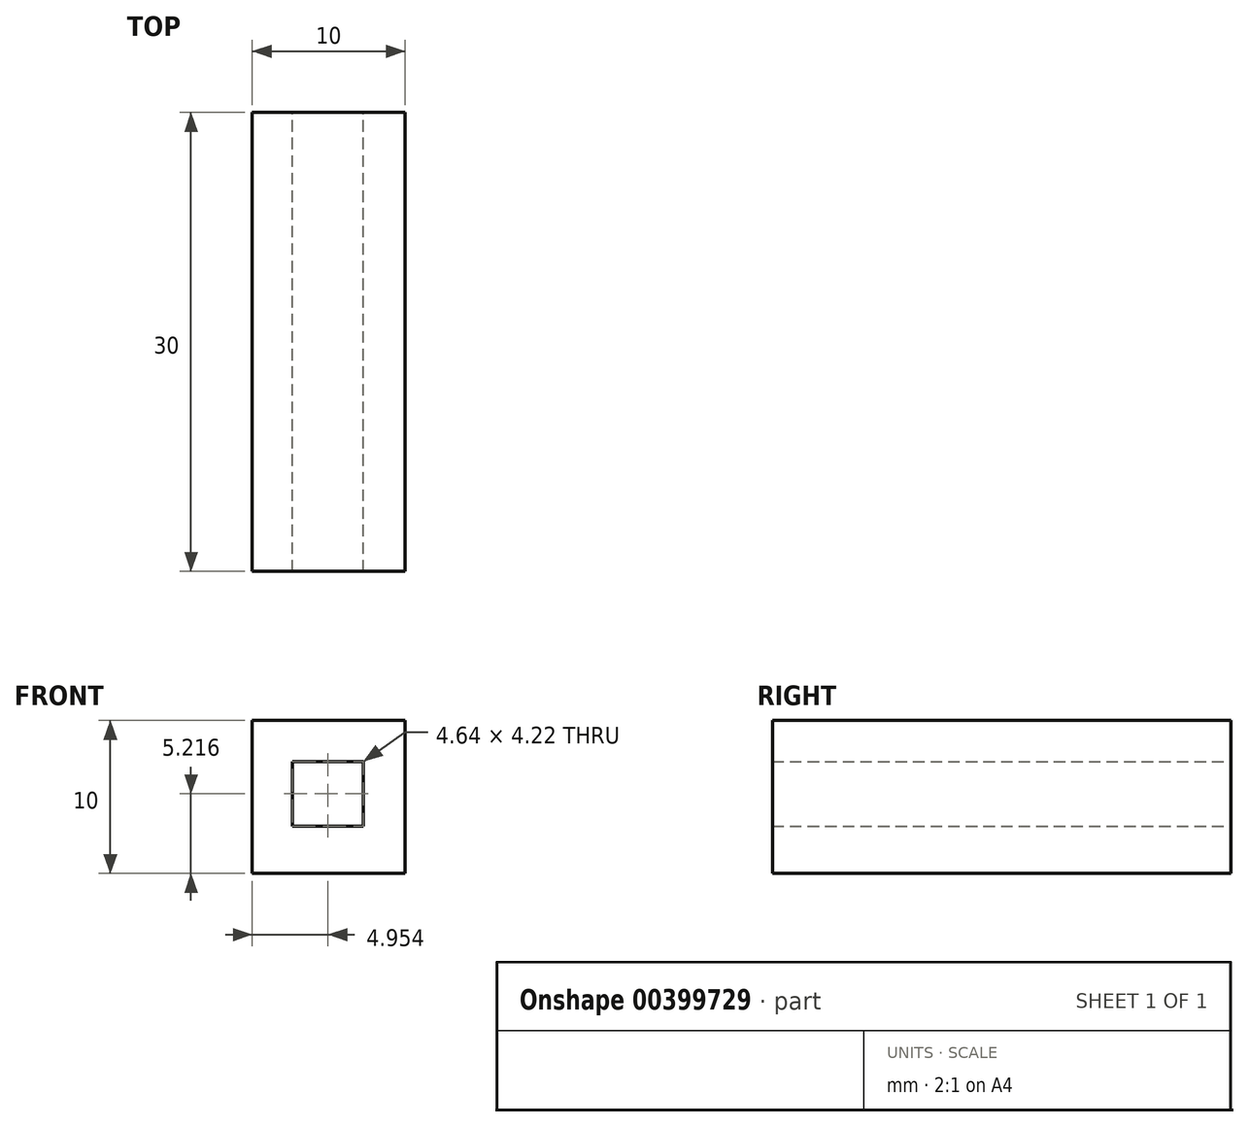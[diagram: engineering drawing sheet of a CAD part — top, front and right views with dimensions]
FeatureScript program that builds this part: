
annotation { "Feature Type Name" : "Feature", "Feature Type Description" : "" }
export const myFeature = defineFeature(function(context is Context, id is Id, definition is map)
    precondition{}
    {
        {
            var Q0;
            Q0=qCreatedBy(makeId("Front.planeOp"),FACE);
            var sketch = newSketch(context, id + "F0", { "sketchPlane" : qUnion([Q0])});
            skLineSegment(sketch, "E0.bottom", {"start": v(-17.14, 25.4) * mm, "end": v(-7.14, 25.4) * mm});
            skLineSegment(sketch, "E0.top", {"start": v(-17.14, 15.4) * mm, "end": v(-7.14, 15.4) * mm});
            skLineSegment(sketch, "E0.left", {"start": v(-17.14, 25.4) * mm, "end": v(-17.14, 15.4) * mm});
            skLineSegment(sketch, "E0.right", {"start": v(-7.14, 25.4) * mm, "end": v(-7.14, 15.4) * mm});
            skLineSegment(sketch, "E1.bottom", {"start": v(-14.5, 22.72) * mm, "end": v(-9.87, 22.72) * mm});
            skLineSegment(sketch, "E1.top", {"start": v(-14.5, 18.5) * mm, "end": v(-9.87, 18.5) * mm});
            skLineSegment(sketch, "E1.left", {"start": v(-14.5, 22.72) * mm, "end": v(-14.5, 18.5) * mm});
            skLineSegment(sketch, "E1.right", {"start": v(-9.87, 22.72) * mm, "end": v(-9.87, 18.5) * mm});
            skSolve(sketch);
        }
        {
            var Q0;
            Q0=makeQuery(id+"F0.imprint","IMPRINT",FACE,{"disambiguationData":[TD([[makeQuery(id+"F0.imprint","IMPRINT",EDGE,{"derivedFrom":sQuery(id+"F0.wireOp",EDGE,"E0.bottom")}),-1.0]])]});
            extrude(context, id + "F1", {"entities" : qUnion([Q0]), "endBound" : BoundingType.SYMMETRIC, "depth" : 30 * mm});
        }
    });
